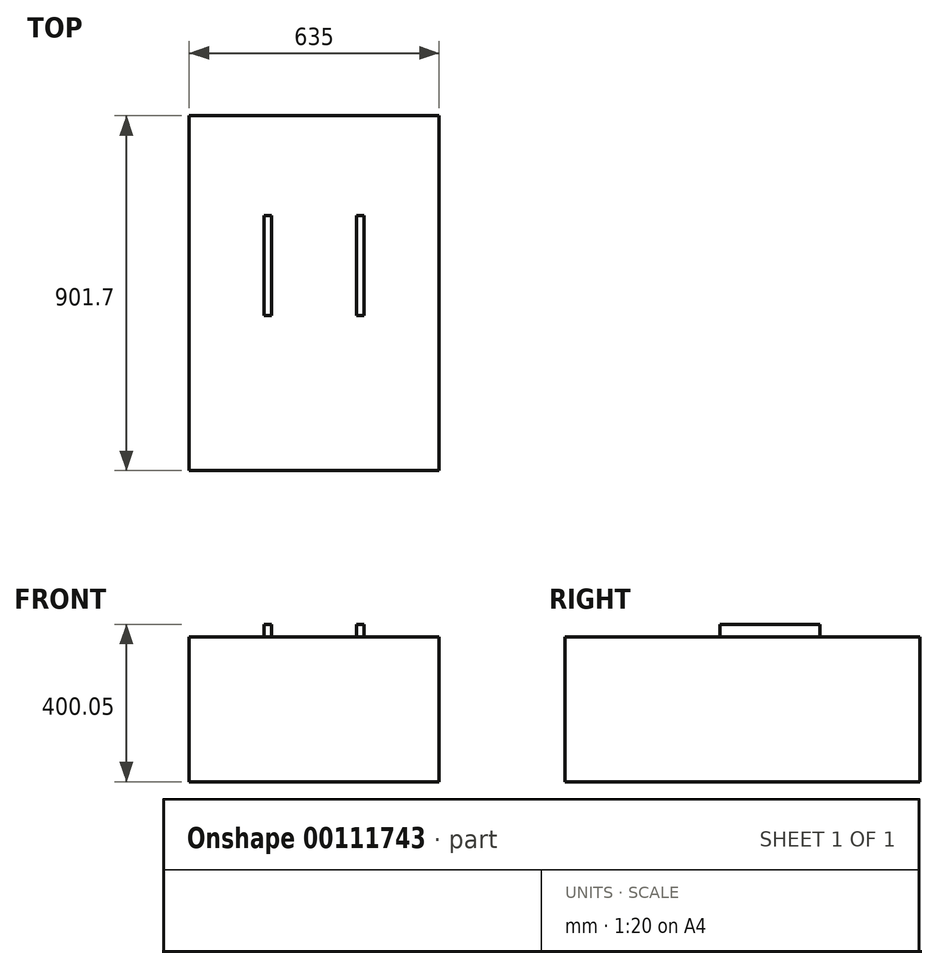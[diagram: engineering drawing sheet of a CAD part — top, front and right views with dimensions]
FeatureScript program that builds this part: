
annotation { "Feature Type Name" : "Feature", "Feature Type Description" : "" }
export const myFeature = defineFeature(function(context is Context, id is Id, definition is map)
    precondition{}
    {
        {
            var Q0;
            Q0=qCreatedBy(makeId("Top.planeOp"),FACE);
            var sketch = newSketch(context, id + "F0", { "sketchPlane" : qUnion([Q0])});
            skLineSegment(sketch, "E0.bottom", {"start": v(-134.7, -72.64) * mm, "end": v(500.3, -72.64) * mm});
            skLineSegment(sketch, "E0.top", {"start": v(-134.7, 829.06) * mm, "end": v(500.3, 829.06) * mm});
            skLineSegment(sketch, "E0.left", {"start": v(-134.7, -72.64) * mm, "end": v(-134.7, 829.06) * mm});
            skLineSegment(sketch, "E0.right", {"start": v(500.3, -72.64) * mm, "end": v(500.3, 829.06) * mm});
            skSolve(sketch);
        }
        {
            var Q0;
            Q0=makeQuery(id+"F0.imprint","IMPRINT",FACE,{"disambiguationData":[TD([[makeQuery(id+"F0.imprint","IMPRINT",EDGE,{"derivedFrom":sQuery(id+"F0.wireOp",EDGE,"E0.bottom")}),1.0]])]});
            extrude(context, id + "F1", {"entities" : qUnion([Q0]), "depth" : 368.3 * mm});
        }
        {
            var Q0;
            Q0=makeQuery(id+"F1.opExtrude","CAP_FACE",FACE,{"disambiguationData":[OSD([sQuery(id+"F0.wireOp",EDGE,"E0.bottom"),sQuery(id+"F0.wireOp",EDGE,"E0.top"),sQuery(id+"F0.wireOp",EDGE,"E0.left"),sQuery(id+"F0.wireOp",EDGE,"E0.right")])],"isStart":false});
            var sketch = newSketch(context, id + "F2", { "sketchPlane" : qUnion([Q0])});
            skLineSegment(sketch, "E1.bottom", {"start": v(55.8, 575.06) * mm, "end": v(74.84, 575.06) * mm});
            skLineSegment(sketch, "E1.top", {"start": v(55.8, 321.06) * mm, "end": v(74.84, 321.06) * mm});
            skLineSegment(sketch, "E1.left", {"start": v(55.8, 575.06) * mm, "end": v(55.8, 321.06) * mm});
            skLineSegment(sketch, "E1.right", {"start": v(74.84, 575.06) * mm, "end": v(74.84, 321.06) * mm});
            skLineSegment(sketch, "E2.bottom", {"start": v(1283.2, 321.06) * mm, "end": v(1578.13, 321.06) * mm});
            skLineSegment(sketch, "E2.top", {"start": v(1283.2, 1762.36) * mm, "end": v(1578.13, 1762.36) * mm});
            skLineSegment(sketch, "E2.left", {"start": v(1283.2, 321.06) * mm, "end": v(1283.2, 1762.36) * mm});
            skLineSegment(sketch, "E2.right", {"start": v(1578.13, 321.06) * mm, "end": v(1578.13, 1762.36) * mm});
            skLineSegment(sketch, "E3.bottom", {"start": v(290.74, 321.06) * mm, "end": v(309.8, 321.06) * mm});
            skLineSegment(sketch, "E3.top", {"start": v(290.74, 575.06) * mm, "end": v(309.8, 575.06) * mm});
            skLineSegment(sketch, "E3.left", {"start": v(290.74, 321.06) * mm, "end": v(290.74, 575.06) * mm});
            skLineSegment(sketch, "E3.right", {"start": v(309.8, 321.06) * mm, "end": v(309.8, 575.06) * mm});
            skSolve(sketch);
        }
        {
            var Q0;
            Q0=makeQuery(id+"F2.imprint","IMPRINT",FACE,{"disambiguationData":[TD([[makeQuery(id+"F2.imprint","IMPRINT",EDGE,{"derivedFrom":sQuery(id+"F2.wireOp",EDGE,"E1.bottom")}),-1.0]])]});
            var Q1;
            Q1=makeQuery(id+"F2.imprint","IMPRINT",FACE,{"disambiguationData":[TD([[makeQuery(id+"F2.imprint","IMPRINT",EDGE,{"derivedFrom":sQuery(id+"F2.wireOp",EDGE,"E3.bottom")}),1.0]])]});
            extrude(context, id + "F3", {"entities" : qUnion([Q0, Q1]), "operationType" : NewBodyOperationType.ADD, "depth" : 31.75 * mm});
        }
    });
